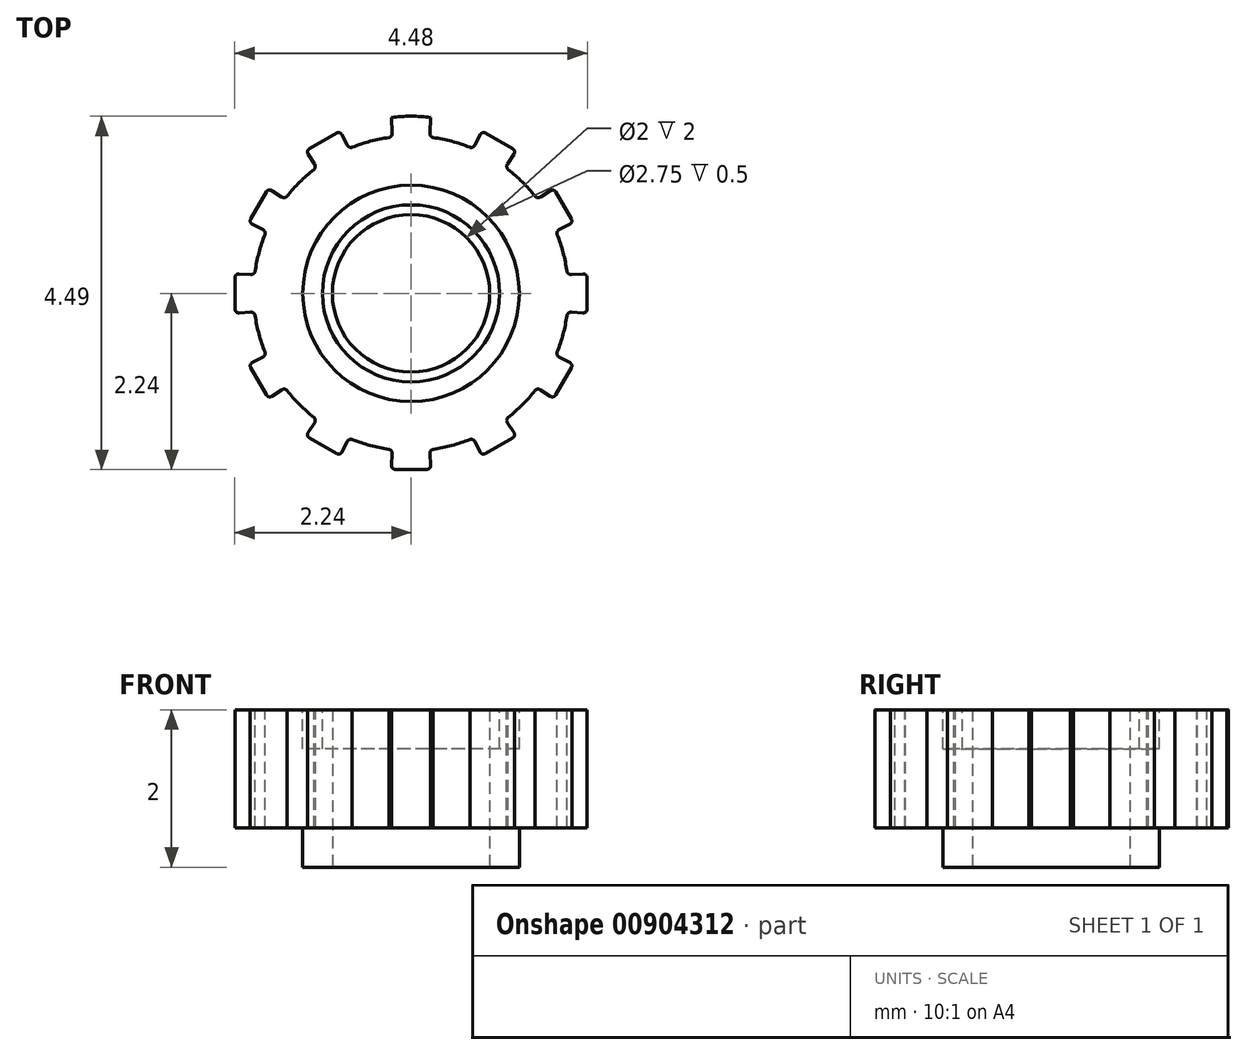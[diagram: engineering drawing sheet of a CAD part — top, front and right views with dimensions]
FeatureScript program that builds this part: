
annotation { "Feature Type Name" : "Feature", "Feature Type Description" : "" }
export const myFeature = defineFeature(function(context is Context, id is Id, definition is map)
    precondition{}
    {
        {
            var Q0;
            Q0=qCreatedBy(makeId("Front.planeOp"),FACE);
            var sketch = newSketch(context, id + "F0", { "sketchPlane" : qUnion([Q0])});
            skLineSegment(sketch, "E0.bottom", {"start": v(0, 0) * mm, "end": v(-2.25, 0) * mm});
            skLineSegment(sketch, "E0.top", {"start": v(0, 2) * mm, "end": v(-2.25, 2) * mm});
            skLineSegment(sketch, "E0.left", {"start": v(0, 0) * mm, "end": v(0, 2) * mm});
            skLineSegment(sketch, "E0.right", {"start": v(-2.25, 0) * mm, "end": v(-2.25, 2) * mm});
            skLineSegment(sketch, "E1", {"start": v(-1, 2) * mm, "end": v(-1, 0) * mm});
            skSolve(sketch);
        }
        {
            var Q0;
            {var subQ0=sQuery(id+"F0.wireOp",EDGE,"E0.right");Q0=makeQuery(id+"F0.imprint","IMPRINT",FACE,{"disambiguationData":[TD([[makeQuery(id+"F0.imprint","IMPRINT",EDGE,{"derivedFrom":subQ0}),-1.0]])]});}
            var Q1;
            Q1=sQuery(id+"F0.wireOp",EDGE,"E0.left");
            revolve(context, id + "F1", {"surfaceOperationType" : NewSurfaceOperationType.NEW, "entities" : qUnion([Q0]), "axis" : qUnion([Q1]), "revolveType" : RevolveType.FULL});
        }
        {
            var Q0;
            Q0=makeQuery(id+"F1.opRevolve","SWEPT_FACE",FACE,{"disambiguationData":[OSD([sQuery(id+"F0.wireOp",EDGE,"E0.top")])]});
            var sketch = newSketch(context, id + "F2", { "sketchPlane" : qUnion([Q0])});
            skLineSegment(sketch, "E2", {"start": v(0, 0) * mm, "end": v(0, 2.25) * mm});
            skLineSegment(sketch, "E3", {"start": v(0, 2.24) * mm, "end": v(-0.25, 2.24) * mm});
            skLineSegment(sketch, "E4", {"start": v(-0.25, 2.24) * mm, "end": v(0.25, 2.24) * mm});
            skLineSegment(sketch, "E5.bottom", {"start": v(0.12, 0) * mm, "end": v(-0.12, 0) * mm});
            skLineSegment(sketch, "E5.top", {"start": v(0.12, 0) * mm, "end": v(-0.12, 0) * mm});
            skLineSegment(sketch, "E5.left", {"start": v(0.12, 0) * mm, "end": v(0.12, 0) * mm});
            skLineSegment(sketch, "E5.right", {"start": v(-0.12, 0) * mm, "end": v(-0.12, 0) * mm});
            skPoint(sketch, "E5.middle", {"position": v(0, 0) * mm});
            skLineSegment(sketch, "E6", {"start": v(-0.25, 2.24) * mm, "end": v(-0.12, 0) * mm});
            skLineSegment(sketch, "E7", {"start": v(0.25, 2.24) * mm, "end": v(0.12, 0) * mm});
            skCircle(sketch, "E8", {"center": v(0, 0) * mm, "radius": 2 * mm});
            skLineSegment(sketch, "E9", {"start": v(-0.25, 2.24) * mm, "end": v(-0.2, 2.24) * mm});
            skLineSegment(sketch, "E10", {"start": v(-0.2, 2.24) * mm, "end": v(0.2, 2.24) * mm});
            skLineSegment(sketch, "E11", {"start": v(0.2, 2.24) * mm, "end": v(0.25, 2.24) * mm});
            skLineSegment(sketch, "E12", {"start": v(-0.2, 2.24) * mm, "end": v(-0.12, 0) * mm});
            skLineSegment(sketch, "E13", {"start": v(0.2, 2.24) * mm, "end": v(0.12, 0) * mm});
            skLineSegment(sketch, "E14", {"start": v(-0.25, 2.19) * mm, "end": v(0.25, 2.19) * mm});
            skLineSegment(sketch, "E15", {"start": v(-0.25, 2.19) * mm, "end": v(-0.3, 2.19) * mm});
            skLineSegment(sketch, "E16", {"start": v(0.25, 2.19) * mm, "end": v(0.3, 2.19) * mm});
            skLineSegment(sketch, "E17", {"start": v(-0.3, 2.19) * mm, "end": v(-0.12, 0) * mm});
            skLineSegment(sketch, "E18", {"start": v(0.3, 2.19) * mm, "end": v(0.12, 0) * mm});
            skLineSegment(sketch, "E19", {"start": v(-0.24, 2.04) * mm, "end": v(0.2, 2.04) * mm});
            skLineSegment(sketch, "E20", {"start": v(0.2, 2.04) * mm, "end": v(0.24, 2.04) * mm});
            skLineSegment(sketch, "E21", {"start": v(0.24, 2.04) * mm, "end": v(-0.2, 2.04) * mm});
            skArc(sketch, "E22", {"start": v(-0.28, 1.98) * mm, "mid": v(-0.25, 2) * mm, "end": v(-0.24, 2.04) * mm});
            skArc(sketch, "E23", {"start": v(-0.2, 2.24) * mm, "mid": v(-0.23, 2.22) * mm, "end": v(-0.25, 2.19) * mm});
            skArc(sketch, "E24", {"start": v(0.25, 2.19) * mm, "mid": v(0.23, 2.22) * mm, "end": v(0.2, 2.24) * mm});
            skArc(sketch, "E25", {"start": v(0.24, 2.04) * mm, "mid": v(0.25, 2) * mm, "end": v(0.28, 1.98) * mm});
            skArc(sketch, "E26.1.0", {"start": v(-1.23, 1.57) * mm, "mid": v(-1.22, 1.6) * mm, "end": v(-1.22, 1.64) * mm});
            skLineSegment(sketch, "E26.1.1", {"start": v(-1.33, 1.81) * mm, "end": v(-0.1, -0.06) * mm});
            skArc(sketch, "E26.1.2", {"start": v(-1.3, 1.84) * mm, "mid": v(-1.31, 1.8) * mm, "end": v(-1.3, 1.77) * mm});
            skLineSegment(sketch, "E26.1.3", {"start": v(-1.33, 1.81) * mm, "end": v(-0.9, 2.06) * mm});
            skArc(sketch, "E26.1.4", {"start": v(-0.88, 2.02) * mm, "mid": v(-0.9, 2.04) * mm, "end": v(-0.94, 2.04) * mm});
            skLineSegment(sketch, "E26.1.5", {"start": v(-0.9, 2.06) * mm, "end": v(0.1, 0.06) * mm});
            skArc(sketch, "E26.1.6", {"start": v(-0.81, 1.88) * mm, "mid": v(-0.78, 1.86) * mm, "end": v(-0.75, 1.86) * mm});
            skArc(sketch, "E26.2.0", {"start": v(-1.86, 0.75) * mm, "mid": v(-1.86, 0.78) * mm, "end": v(-1.88, 0.81) * mm});
            skLineSegment(sketch, "E26.2.1", {"start": v(-2.06, 0.9) * mm, "end": v(-0.06, -0.1) * mm});
            skArc(sketch, "E26.2.2", {"start": v(-2.04, 0.94) * mm, "mid": v(-2.04, 0.9) * mm, "end": v(-2.02, 0.88) * mm});
            skLineSegment(sketch, "E26.2.3", {"start": v(-2.06, 0.9) * mm, "end": v(-1.81, 1.33) * mm});
            skArc(sketch, "E26.2.4", {"start": v(-1.77, 1.3) * mm, "mid": v(-1.8, 1.31) * mm, "end": v(-1.84, 1.3) * mm});
            skLineSegment(sketch, "E26.2.5", {"start": v(-1.81, 1.33) * mm, "end": v(0.06, 0.1) * mm});
            skArc(sketch, "E26.2.6", {"start": v(-1.64, 1.22) * mm, "mid": v(-1.6, 1.22) * mm, "end": v(-1.57, 1.23) * mm});
            skArc(sketch, "E27.2.3.0", {"start": v(-1.98, -0.28) * mm, "mid": v(-2, -0.25) * mm, "end": v(-2.04, -0.24) * mm});
            skLineSegment(sketch, "E27.4.3.0", {"start": v(-2.24, -0.25) * mm, "end": v(0, -0.12) * mm});
            skArc(sketch, "E27.7.3.0", {"start": v(-2.24, -0.2) * mm, "mid": v(-2.22, -0.23) * mm, "end": v(-2.19, -0.25) * mm});
            skLineSegment(sketch, "E27.11.3.0", {"start": v(-2.24, -0.25) * mm, "end": v(-2.24, 0.25) * mm});
            skArc(sketch, "E27.14.3.0", {"start": v(-2.19, 0.25) * mm, "mid": v(-2.22, 0.23) * mm, "end": v(-2.24, 0.2) * mm});
            skLineSegment(sketch, "E27.18.3.0", {"start": v(-2.24, 0.25) * mm, "end": v(0, 0.12) * mm});
            skArc(sketch, "E27.21.3.0", {"start": v(-2.04, 0.24) * mm, "mid": v(-2, 0.25) * mm, "end": v(-1.98, 0.28) * mm});
            skArc(sketch, "E27.2.4.0", {"start": v(-1.57, -1.23) * mm, "mid": v(-1.6, -1.22) * mm, "end": v(-1.64, -1.22) * mm});
            skLineSegment(sketch, "E27.4.4.0", {"start": v(-1.81, -1.33) * mm, "end": v(0.06, -0.1) * mm});
            skArc(sketch, "E27.7.4.0", {"start": v(-1.84, -1.3) * mm, "mid": v(-1.8, -1.31) * mm, "end": v(-1.77, -1.3) * mm});
            skLineSegment(sketch, "E27.11.4.0", {"start": v(-1.81, -1.33) * mm, "end": v(-2.06, -0.9) * mm});
            skArc(sketch, "E27.14.4.0", {"start": v(-2.02, -0.88) * mm, "mid": v(-2.04, -0.9) * mm, "end": v(-2.04, -0.94) * mm});
            skLineSegment(sketch, "E27.18.4.0", {"start": v(-2.06, -0.9) * mm, "end": v(-0.06, 0.1) * mm});
            skArc(sketch, "E27.21.4.0", {"start": v(-1.88, -0.81) * mm, "mid": v(-1.86, -0.78) * mm, "end": v(-1.86, -0.75) * mm});
            skArc(sketch, "E27.2.5.0", {"start": v(-0.75, -1.86) * mm, "mid": v(-0.78, -1.86) * mm, "end": v(-0.81, -1.88) * mm});
            skLineSegment(sketch, "E27.4.5.0", {"start": v(-0.9, -2.06) * mm, "end": v(0.1, -0.06) * mm});
            skArc(sketch, "E27.7.5.0", {"start": v(-0.94, -2.04) * mm, "mid": v(-0.9, -2.04) * mm, "end": v(-0.88, -2.02) * mm});
            skLineSegment(sketch, "E27.11.5.0", {"start": v(-0.9, -2.06) * mm, "end": v(-1.33, -1.81) * mm});
            skArc(sketch, "E27.14.5.0", {"start": v(-1.3, -1.77) * mm, "mid": v(-1.31, -1.8) * mm, "end": v(-1.3, -1.84) * mm});
            skLineSegment(sketch, "E27.18.5.0", {"start": v(-1.33, -1.81) * mm, "end": v(-0.1, 0.06) * mm});
            skArc(sketch, "E27.21.5.0", {"start": v(-1.22, -1.64) * mm, "mid": v(-1.22, -1.6) * mm, "end": v(-1.23, -1.57) * mm});
            skArc(sketch, "E27.2.6.0", {"start": v(0.28, -1.98) * mm, "mid": v(0.25, -2) * mm, "end": v(0.24, -2.04) * mm});
            skLineSegment(sketch, "E27.4.6.0", {"start": v(0.25, -2.24) * mm, "end": v(0.13, 0) * mm});
            skArc(sketch, "E27.7.6.0", {"start": v(0.2, -2.24) * mm, "mid": v(0.23, -2.22) * mm, "end": v(0.25, -2.19) * mm});
            skLineSegment(sketch, "E27.11.6.0", {"start": v(0.25, -2.24) * mm, "end": v(-0.25, -2.24) * mm});
            skArc(sketch, "E27.14.6.0", {"start": v(-0.25, -2.19) * mm, "mid": v(-0.23, -2.22) * mm, "end": v(-0.2, -2.24) * mm});
            skLineSegment(sketch, "E27.18.6.0", {"start": v(-0.25, -2.24) * mm, "end": v(-0.12, 0) * mm});
            skArc(sketch, "E27.21.6.0", {"start": v(-0.24, -2.04) * mm, "mid": v(-0.25, -2) * mm, "end": v(-0.28, -1.98) * mm});
            skArc(sketch, "E27.2.7.0", {"start": v(1.23, -1.57) * mm, "mid": v(1.22, -1.6) * mm, "end": v(1.22, -1.64) * mm});
            skLineSegment(sketch, "E27.4.7.0", {"start": v(1.33, -1.81) * mm, "end": v(0.1, 0.06) * mm});
            skArc(sketch, "E27.7.7.0", {"start": v(1.3, -1.84) * mm, "mid": v(1.31, -1.8) * mm, "end": v(1.3, -1.77) * mm});
            skLineSegment(sketch, "E27.11.7.0", {"start": v(1.33, -1.81) * mm, "end": v(0.9, -2.06) * mm});
            skArc(sketch, "E27.14.7.0", {"start": v(0.88, -2.02) * mm, "mid": v(0.9, -2.04) * mm, "end": v(0.94, -2.04) * mm});
            skLineSegment(sketch, "E27.18.7.0", {"start": v(0.9, -2.06) * mm, "end": v(-0.1, -0.06) * mm});
            skArc(sketch, "E27.21.7.0", {"start": v(0.81, -1.88) * mm, "mid": v(0.78, -1.86) * mm, "end": v(0.75, -1.86) * mm});
            skArc(sketch, "E28.2.8.0", {"start": v(1.86, -0.75) * mm, "mid": v(1.86, -0.78) * mm, "end": v(1.88, -0.81) * mm});
            skLineSegment(sketch, "E28.4.8.0", {"start": v(2.06, -0.9) * mm, "end": v(0.06, 0.1) * mm});
            skArc(sketch, "E28.7.8.0", {"start": v(2.04, -0.94) * mm, "mid": v(2.04, -0.9) * mm, "end": v(2.02, -0.88) * mm});
            skLineSegment(sketch, "E28.11.8.0", {"start": v(2.06, -0.9) * mm, "end": v(1.81, -1.33) * mm});
            skArc(sketch, "E28.14.8.0", {"start": v(1.77, -1.3) * mm, "mid": v(1.8, -1.31) * mm, "end": v(1.84, -1.3) * mm});
            skLineSegment(sketch, "E28.18.8.0", {"start": v(1.81, -1.33) * mm, "end": v(-0.06, -0.1) * mm});
            skArc(sketch, "E28.21.8.0", {"start": v(1.64, -1.22) * mm, "mid": v(1.6, -1.22) * mm, "end": v(1.57, -1.23) * mm});
            skArc(sketch, "E28.2.9.0", {"start": v(1.98, 0.28) * mm, "mid": v(2, 0.25) * mm, "end": v(2.04, 0.24) * mm});
            skLineSegment(sketch, "E28.4.9.0", {"start": v(2.24, 0.25) * mm, "end": v(0, 0.12) * mm});
            skArc(sketch, "E28.7.9.0", {"start": v(2.24, 0.2) * mm, "mid": v(2.22, 0.23) * mm, "end": v(2.19, 0.25) * mm});
            skLineSegment(sketch, "E28.11.9.0", {"start": v(2.24, 0.25) * mm, "end": v(2.24, -0.25) * mm});
            skArc(sketch, "E28.14.9.0", {"start": v(2.19, -0.25) * mm, "mid": v(2.22, -0.23) * mm, "end": v(2.24, -0.2) * mm});
            skLineSegment(sketch, "E28.18.9.0", {"start": v(2.24, -0.25) * mm, "end": v(0, -0.12) * mm});
            skArc(sketch, "E28.21.9.0", {"start": v(2.04, -0.24) * mm, "mid": v(2, -0.25) * mm, "end": v(1.98, -0.28) * mm});
            skArc(sketch, "E29.2.10.0", {"start": v(1.57, 1.23) * mm, "mid": v(1.6, 1.22) * mm, "end": v(1.64, 1.22) * mm});
            skLineSegment(sketch, "E29.4.10.0", {"start": v(1.81, 1.33) * mm, "end": v(-0.06, 0.1) * mm});
            skArc(sketch, "E29.7.10.0", {"start": v(1.84, 1.3) * mm, "mid": v(1.8, 1.31) * mm, "end": v(1.77, 1.3) * mm});
            skLineSegment(sketch, "E29.11.10.0", {"start": v(1.81, 1.33) * mm, "end": v(2.06, 0.9) * mm});
            skArc(sketch, "E29.14.10.0", {"start": v(2.02, 0.88) * mm, "mid": v(2.04, 0.9) * mm, "end": v(2.04, 0.94) * mm});
            skLineSegment(sketch, "E29.18.10.0", {"start": v(2.06, 0.9) * mm, "end": v(0.06, -0.1) * mm});
            skArc(sketch, "E29.21.10.0", {"start": v(1.88, 0.81) * mm, "mid": v(1.86, 0.78) * mm, "end": v(1.86, 0.75) * mm});
            skArc(sketch, "E29.2.11.0", {"start": v(0.75, 1.86) * mm, "mid": v(0.78, 1.86) * mm, "end": v(0.81, 1.88) * mm});
            skLineSegment(sketch, "E29.4.11.0", {"start": v(0.9, 2.06) * mm, "end": v(-0.1, 0.06) * mm});
            skArc(sketch, "E29.7.11.0", {"start": v(0.94, 2.04) * mm, "mid": v(0.9, 2.04) * mm, "end": v(0.88, 2.02) * mm});
            skLineSegment(sketch, "E29.11.11.0", {"start": v(0.9, 2.06) * mm, "end": v(1.33, 1.81) * mm});
            skArc(sketch, "E29.14.11.0", {"start": v(1.3, 1.77) * mm, "mid": v(1.31, 1.8) * mm, "end": v(1.3, 1.84) * mm});
            skLineSegment(sketch, "E29.18.11.0", {"start": v(1.33, 1.81) * mm, "end": v(0.1, -0.06) * mm});
            skArc(sketch, "E29.21.11.0", {"start": v(1.22, 1.64) * mm, "mid": v(1.22, 1.6) * mm, "end": v(1.23, 1.57) * mm});
            skSolve(sketch);
        }
        {
            var Q0;
            {var subQ1=sQuery(id+"F2.wireOp",EDGE,"E15");Q0=makeQuery(id+"F2.imprint","IMPRINT",FACE,{"disambiguationData":[TD([[makeQuery(id+"F2.imprint","IMPRINT",EDGE,{"derivedFrom":subQ1}),-1.0]])]});}
            var Q1;
            {var subQ0=sQuery(id+"F2.wireOp",EDGE,"E15");Q1=makeQuery(id+"F2.imprint","IMPRINT",FACE,{"disambiguationData":[TD([[makeQuery(id+"F2.imprint","IMPRINT",EDGE,{"derivedFrom":subQ0}),1.0]])]});}
            var Q2;
            {var subQ0=sQuery(id+"F2.wireOp",EDGE,"E9");Q2=makeQuery(id+"F2.imprint","IMPRINT",FACE,{"disambiguationData":[TD([[makeQuery(id+"F2.imprint","IMPRINT",EDGE,{"derivedFrom":subQ0}),-1.0]])]});}
            var Q3;
            {var subQ5=sQuery(id+"F2.wireOp",EDGE,"E9");Q3=makeQuery(id+"F2.imprint","IMPRINT",FACE,{"disambiguationData":[TD([[makeQuery(id+"F2.imprint","IMPRINT",EDGE,{"derivedFrom":subQ5}),1.0]])]});}
            var Q4;
            {var subQ5=sQuery(id+"F2.wireOp",EDGE,"E11");Q4=makeQuery(id+"F2.imprint","IMPRINT",FACE,{"disambiguationData":[TD([[makeQuery(id+"F2.imprint","IMPRINT",EDGE,{"derivedFrom":subQ5}),1.0]])]});}
            var Q5;
            {var subQ0=sQuery(id+"F2.wireOp",EDGE,"E11");Q5=makeQuery(id+"F2.imprint","IMPRINT",FACE,{"disambiguationData":[TD([[makeQuery(id+"F2.imprint","IMPRINT",EDGE,{"derivedFrom":subQ0}),-1.0]])]});}
            var Q6;
            {var subQ0=sQuery(id+"F2.wireOp",EDGE,"E16");Q6=makeQuery(id+"F2.imprint","IMPRINT",FACE,{"disambiguationData":[TD([[makeQuery(id+"F2.imprint","IMPRINT",EDGE,{"derivedFrom":subQ0}),1.0]])]});}
            var Q7;
            {var subQ0=sQuery(id+"F2.wireOp",EDGE,"E16");Q7=makeQuery(id+"F2.imprint","IMPRINT",FACE,{"disambiguationData":[TD([[makeQuery(id+"F2.imprint","IMPRINT",EDGE,{"derivedFrom":subQ0}),-1.0]])]});}
            var Q8;
            {var subQ3=sQuery(id+"F2.wireOp",EDGE,"E27.7.7.0");Q8=makeQuery(id+"F2.imprint","IMPRINT",FACE,{"disambiguationData":[TD([[makeQuery(id+"F2.imprint","IMPRINT",EDGE,{"derivedFrom":subQ3}),-1.0]])]});}
            var Q9;
            {var subQ0=sQuery(id+"F2.wireOp",EDGE,"E27.11.7.0");var subQ3=makeQuery(id+"F2.imprint","INTERSECT",VERTEX,{"derivedFrom":[sQuery(id+"F2.wireOp",EDGE,"E27.7.7.0"),subQ0]});Q9=makeQuery(id+"F2.imprint","IMPRINT",FACE,{"disambiguationData":[TD([[makeQuery(id+"F2.imprint","IMPRINT",EDGE,{"disambiguationData":[TD([[subQ3,-1.0]])],"derivedFrom":subQ0}),1.0]])]});}
            var Q10;
            {var subQ3=sQuery(id+"F2.wireOp",EDGE,"E27.14.7.0");Q10=makeQuery(id+"F2.imprint","IMPRINT",FACE,{"disambiguationData":[TD([[makeQuery(id+"F2.imprint","IMPRINT",EDGE,{"derivedFrom":subQ3}),-1.0]])]});}
            var Q11;
            {var subQ4=sQuery(id+"F2.wireOp",EDGE,"E27.2.6.0");Q11=makeQuery(id+"F2.imprint","IMPRINT",FACE,{"disambiguationData":[TD([[makeQuery(id+"F2.imprint","IMPRINT",EDGE,{"derivedFrom":subQ4}),1.0]])]});}
            var Q12;
            {var subQ3=sQuery(id+"F2.wireOp",EDGE,"E27.7.6.0");Q12=makeQuery(id+"F2.imprint","IMPRINT",FACE,{"disambiguationData":[TD([[makeQuery(id+"F2.imprint","IMPRINT",EDGE,{"derivedFrom":subQ3}),-1.0]])]});}
            var Q13;
            {var subQ0=sQuery(id+"F2.wireOp",EDGE,"E27.11.6.0");var subQ3=makeQuery(id+"F2.imprint","INTERSECT",VERTEX,{"derivedFrom":[sQuery(id+"F2.wireOp",EDGE,"E27.7.6.0"),subQ0]});Q13=makeQuery(id+"F2.imprint","IMPRINT",FACE,{"disambiguationData":[TD([[makeQuery(id+"F2.imprint","IMPRINT",EDGE,{"disambiguationData":[TD([[subQ3,-1.0]])],"derivedFrom":subQ0}),1.0]])]});}
            var Q14;
            {var subQ1=sQuery(id+"F2.wireOp",EDGE,"E27.2.5.0");Q14=makeQuery(id+"F2.imprint","IMPRINT",FACE,{"disambiguationData":[TD([[makeQuery(id+"F2.imprint","IMPRINT",EDGE,{"derivedFrom":subQ1}),1.0]])]});}
            var Q15;
            {var subQ3=sQuery(id+"F2.wireOp",EDGE,"E27.14.6.0");Q15=makeQuery(id+"F2.imprint","IMPRINT",FACE,{"disambiguationData":[TD([[makeQuery(id+"F2.imprint","IMPRINT",EDGE,{"derivedFrom":subQ3}),-1.0]])]});}
            var Q16;
            {var subQ0=sQuery(id+"F2.wireOp",EDGE,"E27.11.5.0");var subQ3=makeQuery(id+"F2.imprint","INTERSECT",VERTEX,{"derivedFrom":[sQuery(id+"F2.wireOp",EDGE,"E27.7.5.0"),subQ0]});Q16=makeQuery(id+"F2.imprint","IMPRINT",FACE,{"disambiguationData":[TD([[makeQuery(id+"F2.imprint","IMPRINT",EDGE,{"disambiguationData":[TD([[subQ3,-1.0]])],"derivedFrom":subQ0}),1.0]])]});}
            var Q17;
            {var subQ3=sQuery(id+"F2.wireOp",EDGE,"E27.7.5.0");Q17=makeQuery(id+"F2.imprint","IMPRINT",FACE,{"disambiguationData":[TD([[makeQuery(id+"F2.imprint","IMPRINT",EDGE,{"derivedFrom":subQ3}),-1.0]])]});}
            var Q18;
            {var subQ3=sQuery(id+"F2.wireOp",EDGE,"E27.14.5.0");Q18=makeQuery(id+"F2.imprint","IMPRINT",FACE,{"disambiguationData":[TD([[makeQuery(id+"F2.imprint","IMPRINT",EDGE,{"derivedFrom":subQ3}),-1.0]])]});}
            var Q19;
            {var subQ4=sQuery(id+"F2.wireOp",EDGE,"E27.2.4.0");Q19=makeQuery(id+"F2.imprint","IMPRINT",FACE,{"disambiguationData":[TD([[makeQuery(id+"F2.imprint","IMPRINT",EDGE,{"derivedFrom":subQ4}),1.0]])]});}
            var Q20;
            {var subQ3=sQuery(id+"F2.wireOp",EDGE,"E27.7.4.0");Q20=makeQuery(id+"F2.imprint","IMPRINT",FACE,{"disambiguationData":[TD([[makeQuery(id+"F2.imprint","IMPRINT",EDGE,{"derivedFrom":subQ3}),-1.0]])]});}
            var Q21;
            {var subQ0=sQuery(id+"F2.wireOp",EDGE,"E27.11.4.0");var subQ3=makeQuery(id+"F2.imprint","INTERSECT",VERTEX,{"derivedFrom":[sQuery(id+"F2.wireOp",EDGE,"E27.7.4.0"),subQ0]});Q21=makeQuery(id+"F2.imprint","IMPRINT",FACE,{"disambiguationData":[TD([[makeQuery(id+"F2.imprint","IMPRINT",EDGE,{"disambiguationData":[TD([[subQ3,-1.0]])],"derivedFrom":subQ0}),1.0]])]});}
            var Q22;
            {var subQ3=sQuery(id+"F2.wireOp",EDGE,"E27.14.4.0");Q22=makeQuery(id+"F2.imprint","IMPRINT",FACE,{"disambiguationData":[TD([[makeQuery(id+"F2.imprint","IMPRINT",EDGE,{"derivedFrom":subQ3}),-1.0]])]});}
            var Q23;
            {var subQ1=sQuery(id+"F2.wireOp",EDGE,"E27.2.3.0");Q23=makeQuery(id+"F2.imprint","IMPRINT",FACE,{"disambiguationData":[TD([[makeQuery(id+"F2.imprint","IMPRINT",EDGE,{"derivedFrom":subQ1}),1.0]])]});}
            var Q24;
            {var subQ3=sQuery(id+"F2.wireOp",EDGE,"E27.7.3.0");Q24=makeQuery(id+"F2.imprint","IMPRINT",FACE,{"disambiguationData":[TD([[makeQuery(id+"F2.imprint","IMPRINT",EDGE,{"derivedFrom":subQ3}),-1.0]])]});}
            var Q25;
            {var subQ0=sQuery(id+"F2.wireOp",EDGE,"E27.11.3.0");var subQ3=makeQuery(id+"F2.imprint","INTERSECT",VERTEX,{"derivedFrom":[sQuery(id+"F2.wireOp",EDGE,"E27.7.3.0"),subQ0]});Q25=makeQuery(id+"F2.imprint","IMPRINT",FACE,{"disambiguationData":[TD([[makeQuery(id+"F2.imprint","IMPRINT",EDGE,{"disambiguationData":[TD([[subQ3,-1.0]])],"derivedFrom":subQ0}),1.0]])]});}
            var Q26;
            {var subQ3=sQuery(id+"F2.wireOp",EDGE,"E27.14.3.0");Q26=makeQuery(id+"F2.imprint","IMPRINT",FACE,{"disambiguationData":[TD([[makeQuery(id+"F2.imprint","IMPRINT",EDGE,{"derivedFrom":subQ3}),-1.0]])]});}
            var Q27;
            {var subQ0=sQuery(id+"F2.wireOp",EDGE,"E26.2.3");var subQ3=makeQuery(id+"F2.imprint","INTERSECT",VERTEX,{"derivedFrom":[sQuery(id+"F2.wireOp",EDGE,"E26.2.2"),subQ0]});Q27=makeQuery(id+"F2.imprint","IMPRINT",FACE,{"disambiguationData":[TD([[makeQuery(id+"F2.imprint","IMPRINT",EDGE,{"disambiguationData":[TD([[subQ3,-1.0]])],"derivedFrom":subQ0}),1.0]])]});}
            var Q28;
            {var subQ3=sQuery(id+"F2.wireOp",EDGE,"E26.2.2");Q28=makeQuery(id+"F2.imprint","IMPRINT",FACE,{"disambiguationData":[TD([[makeQuery(id+"F2.imprint","IMPRINT",EDGE,{"derivedFrom":subQ3}),-1.0]])]});}
            var Q29;
            {var subQ1=sQuery(id+"F2.wireOp",EDGE,"E26.2.0");Q29=makeQuery(id+"F2.imprint","IMPRINT",FACE,{"disambiguationData":[TD([[makeQuery(id+"F2.imprint","IMPRINT",EDGE,{"derivedFrom":subQ1}),1.0]])]});}
            var Q30;
            {var subQ3=sQuery(id+"F2.wireOp",EDGE,"E26.2.4");Q30=makeQuery(id+"F2.imprint","IMPRINT",FACE,{"disambiguationData":[TD([[makeQuery(id+"F2.imprint","IMPRINT",EDGE,{"derivedFrom":subQ3}),-1.0]])]});}
            var Q31;
            {var subQ1=sQuery(id+"F2.wireOp",EDGE,"E26.1.0");Q31=makeQuery(id+"F2.imprint","IMPRINT",FACE,{"disambiguationData":[TD([[makeQuery(id+"F2.imprint","IMPRINT",EDGE,{"derivedFrom":subQ1}),1.0]])]});}
            var Q32;
            {var subQ3=sQuery(id+"F2.wireOp",EDGE,"E26.1.2");Q32=makeQuery(id+"F2.imprint","IMPRINT",FACE,{"disambiguationData":[TD([[makeQuery(id+"F2.imprint","IMPRINT",EDGE,{"derivedFrom":subQ3}),-1.0]])]});}
            var Q33;
            {var subQ3=sQuery(id+"F2.wireOp",EDGE,"E26.1.4");Q33=makeQuery(id+"F2.imprint","IMPRINT",FACE,{"disambiguationData":[TD([[makeQuery(id+"F2.imprint","IMPRINT",EDGE,{"derivedFrom":subQ3}),-1.0]])]});}
            var Q34;
            {var subQ0=sQuery(id+"F2.wireOp",EDGE,"E26.1.3");var subQ3=makeQuery(id+"F2.imprint","INTERSECT",VERTEX,{"derivedFrom":[sQuery(id+"F2.wireOp",EDGE,"E26.1.2"),subQ0]});Q34=makeQuery(id+"F2.imprint","IMPRINT",FACE,{"disambiguationData":[TD([[makeQuery(id+"F2.imprint","IMPRINT",EDGE,{"disambiguationData":[TD([[subQ3,-1.0]])],"derivedFrom":subQ0}),1.0]])]});}
            var Q35;
            {var subQ1=sQuery(id+"F2.wireOp",EDGE,"E27.2.7.0");Q35=makeQuery(id+"F2.imprint","IMPRINT",FACE,{"disambiguationData":[TD([[makeQuery(id+"F2.imprint","IMPRINT",EDGE,{"derivedFrom":subQ1}),1.0]])]});}
            var Q36;
            {var subQ3=sQuery(id+"F2.wireOp",EDGE,"E28.14.8.0");Q36=makeQuery(id+"F2.imprint","IMPRINT",FACE,{"disambiguationData":[TD([[makeQuery(id+"F2.imprint","IMPRINT",EDGE,{"derivedFrom":subQ3}),-1.0]])]});}
            var Q37;
            {var subQ0=sQuery(id+"F2.wireOp",EDGE,"E28.11.8.0");var subQ3=makeQuery(id+"F2.imprint","INTERSECT",VERTEX,{"derivedFrom":[sQuery(id+"F2.wireOp",EDGE,"E28.7.8.0"),subQ0]});Q37=makeQuery(id+"F2.imprint","IMPRINT",FACE,{"disambiguationData":[TD([[makeQuery(id+"F2.imprint","IMPRINT",EDGE,{"disambiguationData":[TD([[subQ3,-1.0]])],"derivedFrom":subQ0}),1.0]])]});}
            var Q38;
            {var subQ3=sQuery(id+"F2.wireOp",EDGE,"E28.7.8.0");Q38=makeQuery(id+"F2.imprint","IMPRINT",FACE,{"disambiguationData":[TD([[makeQuery(id+"F2.imprint","IMPRINT",EDGE,{"derivedFrom":subQ3}),-1.0]])]});}
            var Q39;
            {var subQ1=sQuery(id+"F2.wireOp",EDGE,"E28.2.8.0");Q39=makeQuery(id+"F2.imprint","IMPRINT",FACE,{"disambiguationData":[TD([[makeQuery(id+"F2.imprint","IMPRINT",EDGE,{"derivedFrom":subQ1}),1.0]])]});}
            var Q40;
            {var subQ3=sQuery(id+"F2.wireOp",EDGE,"E28.14.9.0");Q40=makeQuery(id+"F2.imprint","IMPRINT",FACE,{"disambiguationData":[TD([[makeQuery(id+"F2.imprint","IMPRINT",EDGE,{"derivedFrom":subQ3}),-1.0]])]});}
            var Q41;
            {var subQ0=sQuery(id+"F2.wireOp",EDGE,"E28.11.9.0");var subQ3=makeQuery(id+"F2.imprint","INTERSECT",VERTEX,{"derivedFrom":[sQuery(id+"F2.wireOp",EDGE,"E28.7.9.0"),subQ0]});Q41=makeQuery(id+"F2.imprint","IMPRINT",FACE,{"disambiguationData":[TD([[makeQuery(id+"F2.imprint","IMPRINT",EDGE,{"disambiguationData":[TD([[subQ3,-1.0]])],"derivedFrom":subQ0}),1.0]])]});}
            var Q42;
            {var subQ3=sQuery(id+"F2.wireOp",EDGE,"E28.7.9.0");Q42=makeQuery(id+"F2.imprint","IMPRINT",FACE,{"disambiguationData":[TD([[makeQuery(id+"F2.imprint","IMPRINT",EDGE,{"derivedFrom":subQ3}),-1.0]])]});}
            var Q43;
            {var subQ0=sQuery(id+"F2.wireOp",EDGE,"E29.11.11.0");var subQ3=makeQuery(id+"F2.imprint","INTERSECT",VERTEX,{"derivedFrom":[sQuery(id+"F2.wireOp",EDGE,"E29.7.11.0"),subQ0]});Q43=makeQuery(id+"F2.imprint","IMPRINT",FACE,{"disambiguationData":[TD([[makeQuery(id+"F2.imprint","IMPRINT",EDGE,{"disambiguationData":[TD([[subQ3,-1.0]])],"derivedFrom":subQ0}),1.0]])]});}
            var Q44;
            {var subQ3=sQuery(id+"F2.wireOp",EDGE,"E29.7.11.0");Q44=makeQuery(id+"F2.imprint","IMPRINT",FACE,{"disambiguationData":[TD([[makeQuery(id+"F2.imprint","IMPRINT",EDGE,{"derivedFrom":subQ3}),-1.0]])]});}
            var Q45;
            {var subQ3=sQuery(id+"F2.wireOp",EDGE,"E29.14.11.0");Q45=makeQuery(id+"F2.imprint","IMPRINT",FACE,{"disambiguationData":[TD([[makeQuery(id+"F2.imprint","IMPRINT",EDGE,{"derivedFrom":subQ3}),-1.0]])]});}
            var Q46;
            {var subQ1=sQuery(id+"F2.wireOp",EDGE,"E29.2.10.0");Q46=makeQuery(id+"F2.imprint","IMPRINT",FACE,{"disambiguationData":[TD([[makeQuery(id+"F2.imprint","IMPRINT",EDGE,{"derivedFrom":subQ1}),1.0]])]});}
            var Q47;
            {var subQ0=sQuery(id+"F2.wireOp",EDGE,"E29.11.10.0");var subQ3=makeQuery(id+"F2.imprint","INTERSECT",VERTEX,{"derivedFrom":[sQuery(id+"F2.wireOp",EDGE,"E29.7.10.0"),subQ0]});Q47=makeQuery(id+"F2.imprint","IMPRINT",FACE,{"disambiguationData":[TD([[makeQuery(id+"F2.imprint","IMPRINT",EDGE,{"disambiguationData":[TD([[subQ3,-1.0]])],"derivedFrom":subQ0}),1.0]])]});}
            var Q48;
            {var subQ3=sQuery(id+"F2.wireOp",EDGE,"E29.7.10.0");Q48=makeQuery(id+"F2.imprint","IMPRINT",FACE,{"disambiguationData":[TD([[makeQuery(id+"F2.imprint","IMPRINT",EDGE,{"derivedFrom":subQ3}),-1.0]])]});}
            var Q49;
            {var subQ3=sQuery(id+"F2.wireOp",EDGE,"E29.14.10.0");Q49=makeQuery(id+"F2.imprint","IMPRINT",FACE,{"disambiguationData":[TD([[makeQuery(id+"F2.imprint","IMPRINT",EDGE,{"derivedFrom":subQ3}),-1.0]])]});}
            var Q50;
            {var subQ1=sQuery(id+"F2.wireOp",EDGE,"E28.2.9.0");Q50=makeQuery(id+"F2.imprint","IMPRINT",FACE,{"disambiguationData":[TD([[makeQuery(id+"F2.imprint","IMPRINT",EDGE,{"derivedFrom":subQ1}),1.0]])]});}
            extrude(context, id + "F3", {"entities" : qUnion([Q0, Q1, Q2, Q3, Q4, Q5, Q6, Q7, Q8, Q9, Q10, Q11, Q12, Q13, Q14, Q15, Q16, Q17, Q18, Q19, Q20, Q21, Q22, Q23, Q24, Q25, Q26, Q27, Q28, Q29, Q30, Q31, Q32, Q33, Q34, Q35, Q36, Q37, Q38, Q39, Q40, Q41, Q42, Q43, Q44, Q45, Q46, Q47, Q48, Q49, Q50]), "operationType" : NewBodyOperationType.REMOVE, "oppositeDirection" : true, "depth" : 25 * mm, "offsetDistance" : 25 * mm});
        }
        {
            var Q0;
            Q0=makeQuery(id+"F1.opRevolve","SWEPT_FACE",FACE,{"disambiguationData":[OSD([sQuery(id+"F0.wireOp",EDGE,"E0.top")])]});
            var sketch = newSketch(context, id + "F4", { "sketchPlane" : qUnion([Q0])});
            skCircle(sketch, "E30", {"center": v(0, 0) * mm, "radius": 1.13 * mm});
            skCircle(sketch, "E31", {"center": v(0, 0) * mm, "radius": 1.38 * mm});
            skSolve(sketch);
        }
        {
            var Q0;
            Q0=makeQuery(id+"F1.opRevolve","SWEPT_FACE",FACE,{"disambiguationData":[OSD([sQuery(id+"F0.wireOp",EDGE,"E0.bottom")])]});
            var sketch = newSketch(context, id + "F5", { "sketchPlane" : qUnion([Q0])});
            skCircle(sketch, "E32.0", {"center": v(0, 0) * mm, "radius": 1.38 * mm});
            skCircle(sketch, "E32.1", {"center": v(0, 0) * mm, "radius": 1.13 * mm});
            skSolve(sketch);
        }
        {
            var Q0;
            Q0=makeQuery(id+"F5.imprint","IMPRINT",FACE,{"disambiguationData":[TD([[makeQuery(id+"F5.imprint","IMPRINT",EDGE,{"derivedFrom":sQuery(id+"F5.wireOp",EDGE,"E32.0")}),-1.0]])]});
            extrude(context, id + "F6", {"entities" : qUnion([Q0]), "operationType" : NewBodyOperationType.REMOVE, "oppositeDirection" : true, "depth" : 0.5 * mm, "offsetDistance" : 25 * mm});
        }
        {
            var Q0;
            Q0=makeQuery(id+"F4.imprint","IMPRINT",FACE,{"disambiguationData":[TD([[makeQuery(id+"F4.imprint","IMPRINT",EDGE,{"derivedFrom":sQuery(id+"F4.wireOp",EDGE,"E30")}),-1.0]])]});
            extrude(context, id + "F7", {"entities" : qUnion([Q0]), "operationType" : NewBodyOperationType.REMOVE, "oppositeDirection" : true, "depth" : 0.5 * mm, "offsetDistance" : 25 * mm});
        }
    });
